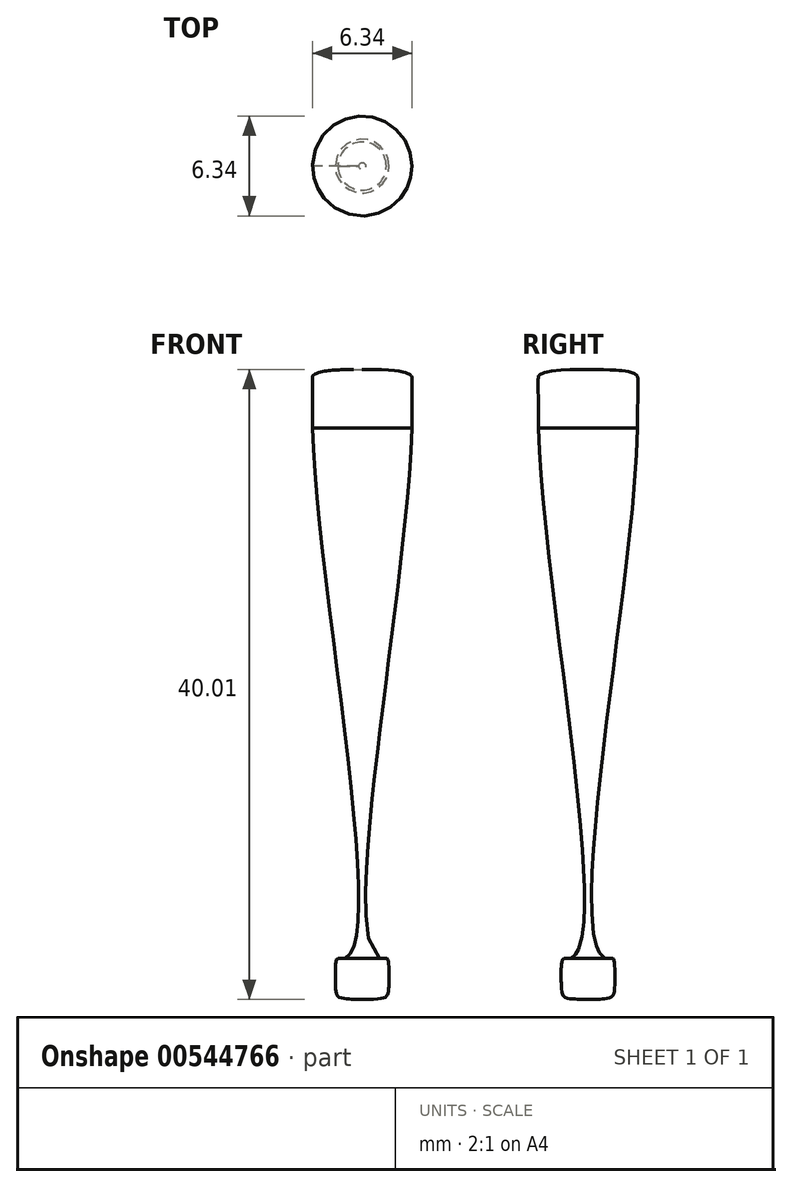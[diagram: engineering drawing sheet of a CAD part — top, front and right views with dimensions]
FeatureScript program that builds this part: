
annotation { "Feature Type Name" : "Feature", "Feature Type Description" : "" }
export const myFeature = defineFeature(function(context is Context, id is Id, definition is map)
    precondition{}
    {
        {
            var Q0;
            Q0=qCreatedBy(makeId("Front.planeOp"),FACE);
            var sketch = newSketch(context, id + "F0", { "sketchPlane" : qUnion([Q0])});
            skLineSegment(sketch, "E0", {"start": v(0, 0) * mm, "end": v(0, 40) * mm});
            skFitSpline(sketch, "E1", {"points": [v(0, 40) * mm, v(3.09, 39.65) * mm, v(3.15, 36.3) * mm], "startDerivative": vector(16.43, 0.36) * mm, "endDerivative": vector(-0.06, -20.71) * mm});
            skFitSpline(sketch, "E2", {"points": [v(0, 0) * mm, v(1.69, 0.73) * mm, v(1.53, 2.62) * mm], "startDerivative": vector(9.76, 0) * mm, "endDerivative": vector(-1.33, 0.09) * mm});
            skFitSpline(sketch, "E3", {"points": [v(1.53, 2.62) * mm, v(3.15, 36.3) * mm], "startDerivative": vector(-10.9, -3.43) * mm, "endDerivative": vector(0.61, 30.74) * mm});
            skSolve(sketch);
        }
        {
            var Q0;
            Q0=makeQuery(id+"F0.imprint","IMPRINT",FACE,{"disambiguationData":[TD([[makeQuery(id+"F0.imprint","IMPRINT",EDGE,{"derivedFrom":sQuery(id+"F0.wireOp",EDGE,"E0")}),-1.0]])]});
            var Q1;
            Q1=sQuery(id+"F0.wireOp",EDGE,"E0");
            revolve(context, id + "F1", {"entities" : qUnion([Q0]), "axis" : qUnion([Q1]), "revolveType" : RevolveType.FULL});
        }
    });
